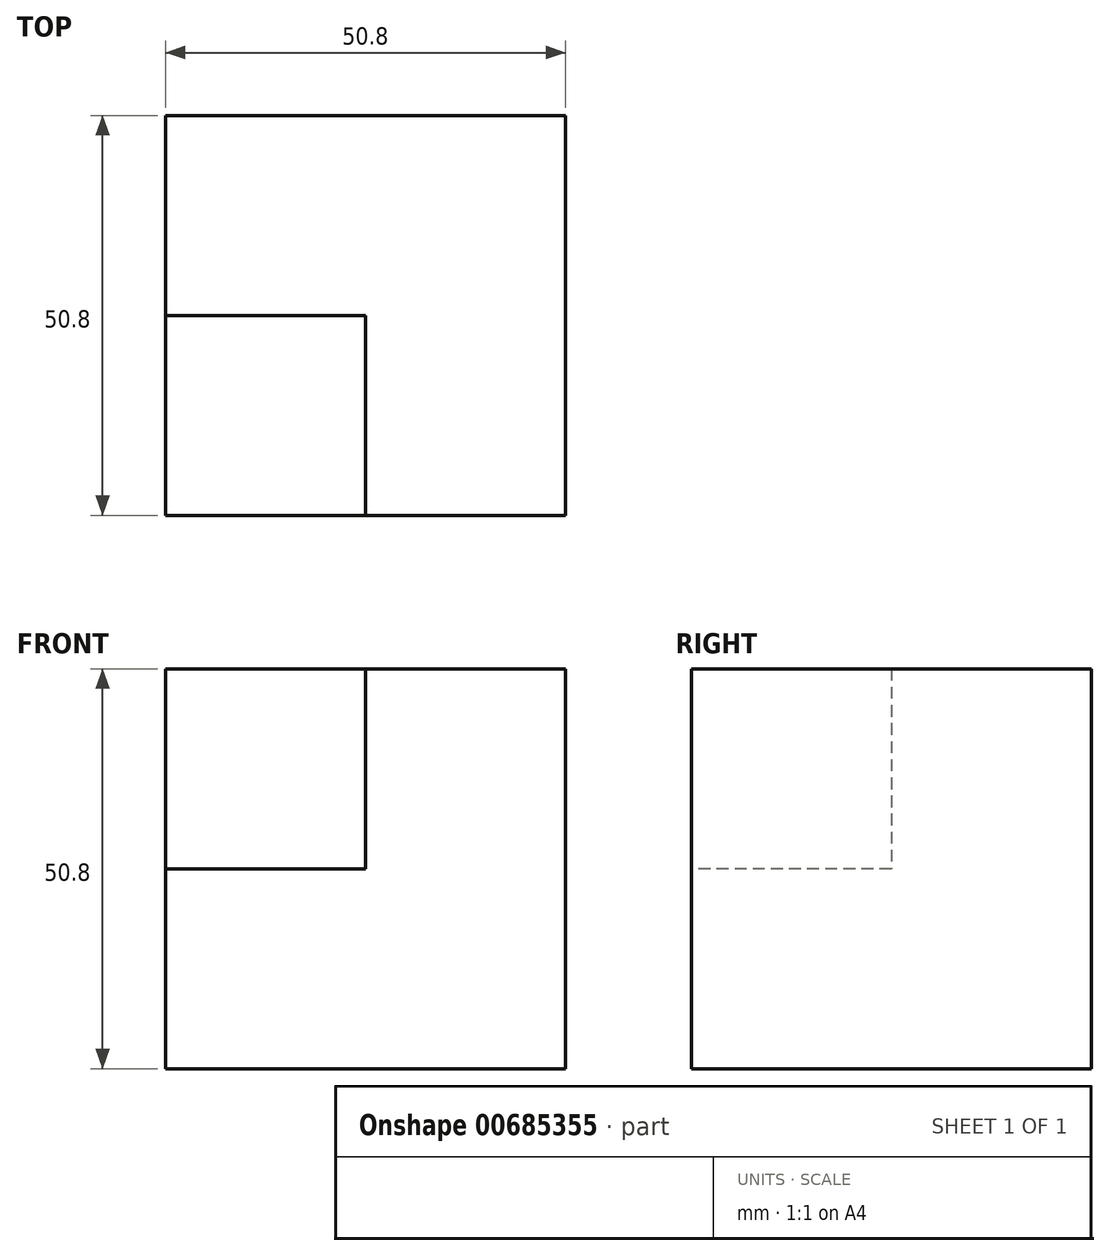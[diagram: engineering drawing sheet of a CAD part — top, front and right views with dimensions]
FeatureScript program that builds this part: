
annotation { "Feature Type Name" : "Feature", "Feature Type Description" : "" }
export const myFeature = defineFeature(function(context is Context, id is Id, definition is map)
    precondition{}
    {
        {
            var Q0;
            Q0=qCreatedBy(makeId("Front.planeOp"),FACE);
            var sketch = newSketch(context, id + "F0", { "sketchPlane" : qUnion([Q0])});
            skLineSegment(sketch, "E0", {"start": v(0, 0) * mm, "end": v(0, -50.8) * mm});
            skLineSegment(sketch, "E1", {"start": v(0, -50.8) * mm, "end": v(50.8, -50.8) * mm});
            skLineSegment(sketch, "E2", {"start": v(50.8, -50.8) * mm, "end": v(50.8, 0) * mm});
            skLineSegment(sketch, "E3", {"start": v(0, 0) * mm, "end": v(50.8, 0) * mm});
            skSolve(sketch);
        }
        {
            var Q0;
            Q0=makeQuery(id+"F0.imprint","IMPRINT",FACE,{"disambiguationData":[TD([[makeQuery(id+"F0.imprint","IMPRINT",EDGE,{"derivedFrom":sQuery(id+"F0.wireOp",EDGE,"E0")}),1.0]])]});
            extrude(context, id + "F1", {"entities" : qUnion([Q0]), "depth" : 50.8 * mm, "offsetDistance" : 25.4 * mm});
        }
        {
            var Q0;
            Q0=makeQuery(id+"F1.opExtrude","CAP_FACE",FACE,{"disambiguationData":[OSD([sQuery(id+"F0.wireOp",EDGE,"E0"),sQuery(id+"F0.wireOp",EDGE,"E1"),sQuery(id+"F0.wireOp",EDGE,"E2"),sQuery(id+"F0.wireOp",EDGE,"E3")])],"isStart":false});
            var sketch = newSketch(context, id + "F2", { "sketchPlane" : qUnion([Q0])});
            skPoint(sketch, "E4.oppositeSnap0", {"position": v(0, -25.4) * mm});
            skLineSegment(sketch, "E4.bottom", {"start": v(0, 0) * mm, "end": v(25.4, 0) * mm});
            skLineSegment(sketch, "E4.top", {"start": v(0, -25.4) * mm, "end": v(25.4, -25.4) * mm});
            skLineSegment(sketch, "E4.left", {"start": v(0, 0) * mm, "end": v(0, -25.4) * mm});
            skLineSegment(sketch, "E4.right", {"start": v(25.4, 0) * mm, "end": v(25.4, -25.4) * mm});
            skSolve(sketch);
        }
        {
            var Q0;
            Q0=makeQuery(id+"F2.imprint","IMPRINT",FACE,{"disambiguationData":[TD([[makeQuery(id+"F2.imprint","IMPRINT",EDGE,{"derivedFrom":sQuery(id+"F2.wireOp",EDGE,"E4.bottom")}),-1.0]])]});
            extrude(context, id + "F3", {"entities" : qUnion([Q0]), "operationType" : NewBodyOperationType.REMOVE, "oppositeDirection" : true, "depth" : 25.4 * mm, "offsetDistance" : 25.4 * mm});
        }
    });
